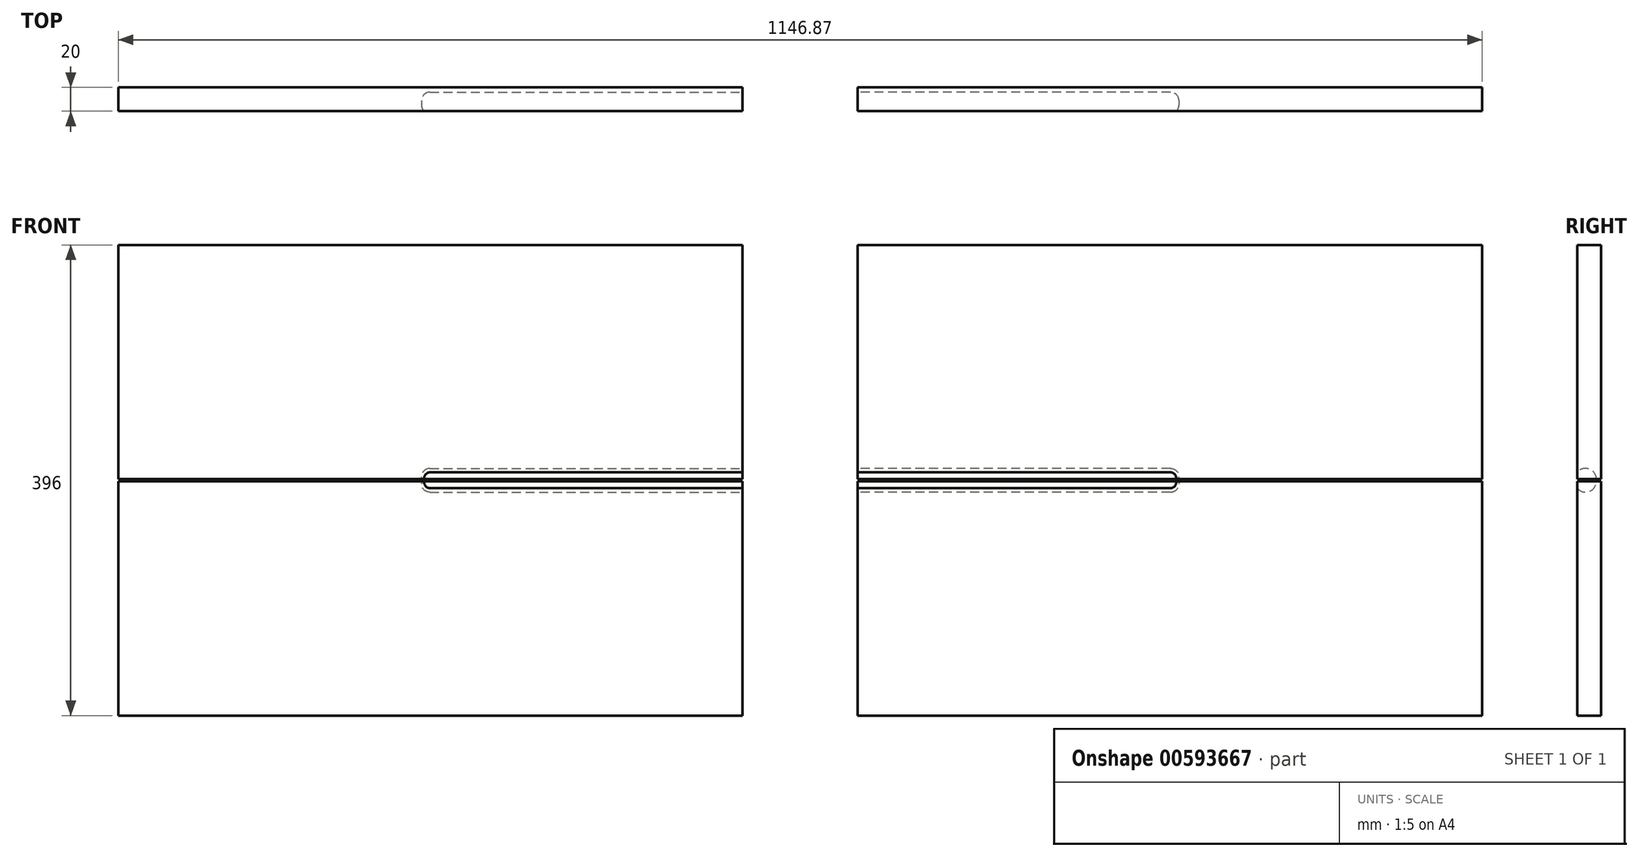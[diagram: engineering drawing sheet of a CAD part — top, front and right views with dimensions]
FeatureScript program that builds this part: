
annotation { "Feature Type Name" : "Feature", "Feature Type Description" : "" }
export const myFeature = defineFeature(function(context is Context, id is Id, definition is map)
    precondition{}
    {
        {
            var Q0;
            Q0=qCreatedBy(makeId("Front.planeOp"),FACE);
            var sketch = newSketch(context, id + "F0", { "sketchPlane" : qUnion([Q0])});
            skLineSegment(sketch, "E0.bottom", {"start": v(-261.44, 123.72) * mm, "end": v(263.56, 123.72) * mm});
            skLineSegment(sketch, "E0.top", {"start": v(-261.44, -73.28) * mm, "end": v(263.56, -73.28) * mm});
            skLineSegment(sketch, "E0.left", {"start": v(-261.44, 123.72) * mm, "end": v(-261.44, -73.28) * mm});
            skLineSegment(sketch, "E0.right", {"start": v(263.56, 123.72) * mm, "end": v(263.56, -73.28) * mm});
            skSolve(sketch);
        }
        {
            var Q0;
            Q0=makeQuery(id+"F0.imprint","IMPRINT",FACE,{"disambiguationData":[TD([[makeQuery(id+"F0.imprint","IMPRINT",EDGE,{"derivedFrom":sQuery(id+"F0.wireOp",EDGE,"E0.bottom")}),-1.0]])]});
            extrude(context, id + "F1", {"entities" : qUnion([Q0]), "oppositeDirection" : true, "depth" : 20 * mm, "offsetDistance" : 25 * mm});
        }
        {
            var Q0;
            Q0=makeQuery(id+"F1.opExtrude","SWEPT_FACE",FACE,{"disambiguationData":[OSD([sQuery(id+"F0.wireOp",EDGE,"E0.right")])]});
            var sketch = newSketch(context, id + "F2", { "sketchPlane" : qUnion([Q0])});
            skCircle(sketch, "E1", {"center": v(7, -73.28) * mm, "radius": 9 * mm});
            skSolve(sketch);
        }
        {
            var Q0;
            {var subQ0=sQuery(id+"F2.wireOp",EDGE,"E1");var subQ1=sQuery(id+"F0.wireOp",EDGE,"E0.right");var subQ4=makeQuery(id+"F1.opExtrude","CAP_EDGE",EDGE,{"disambiguationData":[OSD([subQ1])],"isStart":true});var subQ5=makeQuery(id+"F2.imprint","INTERSECT",VERTEX,{"derivedFrom":[subQ4,subQ0]});Q0=makeQuery(id+"F2.imprint","IMPRINT",FACE,{"disambiguationData":[TD([[makeQuery(id+"F2.imprint","IMPRINT",EDGE,{"disambiguationData":[TD([[subQ5,-1.0]])],"derivedFrom":subQ0}),1.0]])]});}
            var Q1;
            {var subQ0=sQuery(id+"F2.wireOp",EDGE,"E1");var subQ1=sQuery(id+"F0.wireOp",EDGE,"E0.right");var subQ4=makeQuery(id+"F1.opExtrude","CAP_EDGE",EDGE,{"disambiguationData":[OSD([subQ1])],"isStart":true});var subQ5=makeQuery(id+"F2.imprint","INTERSECT",VERTEX,{"derivedFrom":[subQ4,subQ0]});Q1=makeQuery(id+"F2.imprint","IMPRINT",FACE,{"disambiguationData":[TD([[makeQuery(id+"F2.imprint","IMPRINT",EDGE,{"disambiguationData":[TD([[subQ5,1.0]])],"derivedFrom":subQ0}),1.0]])]});}
            extrude(context, id + "F3", {"entities" : qUnion([Q0, Q1]), "operationType" : NewBodyOperationType.REMOVE, "oppositeDirection" : true, "depth" : 270 * mm, "offsetDistance" : 25 * mm});
        }
        {
            var Q0;
            Q0=makeQuery(id+"F3.boolean.opBoolean","COPY",EDGE,{"derivedFrom":makeQuery(id+"F3.opExtrude","CAP_EDGE",EDGE,{"disambiguationData":[OSD([sQuery(id+"F2.wireOp",EDGE,"E1")])],"isStart":false})});
            fillet(context, id + "F4", {"entities" : qUnion([Q0]), "radius" : 7 * mm, "tangentPropagation" : true, "allowEdgeOverflow" : false});
        }
        {
            var Q0;
            Q0=makeQuery(id+"F1.opExtrude","CAP_FACE",FACE,{"disambiguationData":[OSD([sQuery(id+"F0.wireOp",EDGE,"E0.bottom"),sQuery(id+"F0.wireOp",EDGE,"E0.top"),sQuery(id+"F0.wireOp",EDGE,"E0.left"),sQuery(id+"F0.wireOp",EDGE,"E0.right")])],"isStart":true});
            var sketch = newSketch(context, id + "F5", { "sketchPlane" : qUnion([Q0])});
            skLineSegment(sketch, "E2", {"start": v(-94.07, -74.28) * mm, "end": v(-12.9, -74.28) * mm});
            skSolve(sketch);
        }
        {
            var Q0;
            Q0=sQuery(id+"F5.wireOp",EDGE,"E2");
            extrude(context, id + "F6", {"bodyType" : ToolBodyType.SURFACE, "surfaceEntities" : qUnion([Q0]), "oppositeDirection" : true, "depth" : 50 * mm, "offsetDistance" : 25 * mm});
        }
        {
            var Q0;
            Q0=makeQuery(id+"F1.opExtrude","SWEPT_BODY",BODY,{"disambiguationData":[OSD([sQuery(id+"F0.wireOp",EDGE,"E0.bottom"),sQuery(id+"F0.wireOp",EDGE,"E0.top"),sQuery(id+"F0.wireOp",EDGE,"E0.left"),sQuery(id+"F0.wireOp",EDGE,"E0.right")])]});
            var Q1;
            Q1=makeQuery(id+"F6.opExtrude","SWEPT_FACE",FACE,{"disambiguationData":[OSD([sQuery(id+"F5.wireOp",EDGE,"E2")])]});
            mirror(context, id + "F7", {"entities" : qUnion([Q0]), "mirrorPlane" : qUnion([Q1])});
        }
        {
            var Q0;
            Q0=makeQuery(id+"F1.opExtrude","CAP_FACE",FACE,{"disambiguationData":[OSD([sQuery(id+"F0.wireOp",EDGE,"E0.bottom"),sQuery(id+"F0.wireOp",EDGE,"E0.top"),sQuery(id+"F0.wireOp",EDGE,"E0.left"),sQuery(id+"F0.wireOp",EDGE,"E0.right")])],"isStart":true});
            var sketch = newSketch(context, id + "F8", { "sketchPlane" : qUnion([Q0])});
            skLineSegment(sketch, "E3", {"start": v(312, 37.87) * mm, "end": v(312, -154.43) * mm});
            skSolve(sketch);
        }
        {
            var Q0;
            Q0=sQuery(id+"F8.wireOp",EDGE,"E3");
            extrude(context, id + "F9", {"bodyType" : ToolBodyType.SURFACE, "surfaceEntities" : qUnion([Q0]), "oppositeDirection" : true, "depth" : 25 * mm, "offsetDistance" : 25 * mm});
        }
        {
            var Q0;
            Q0=makeQuery(id+"F1.opExtrude","SWEPT_BODY",BODY,{"disambiguationData":[OSD([sQuery(id+"F0.wireOp",EDGE,"E0.bottom"),sQuery(id+"F0.wireOp",EDGE,"E0.top"),sQuery(id+"F0.wireOp",EDGE,"E0.left"),sQuery(id+"F0.wireOp",EDGE,"E0.right")])]});
            var Q1;
            Q1=makeQuery(id+"F7.opPattern","COPY",BODY,{"derivedFrom":makeQuery(id+"F1.opExtrude","SWEPT_BODY",BODY,{"disambiguationData":[OSD([sQuery(id+"F0.wireOp",EDGE,"E0.bottom"),sQuery(id+"F0.wireOp",EDGE,"E0.top"),sQuery(id+"F0.wireOp",EDGE,"E0.left"),sQuery(id+"F0.wireOp",EDGE,"E0.right")])]}),"instanceName":"1"});
            var Q2;
            Q2=makeQuery(id+"F9.opExtrude","SWEPT_FACE",FACE,{"disambiguationData":[OSD([sQuery(id+"F8.wireOp",EDGE,"E3")])]});
            mirror(context, id + "F10", {"entities" : qUnion([Q0, Q1]), "mirrorPlane" : qUnion([Q2])});
        }
    });
